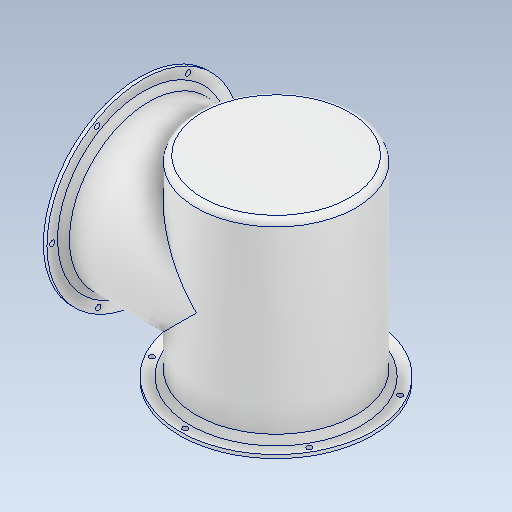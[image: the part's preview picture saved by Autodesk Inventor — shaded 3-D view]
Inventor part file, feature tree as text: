
AUTODESK INVENTOR PART (.ipt)
format: ipt  version: 2021 (Build 250183000, 183)  size: 356,352 bytes
history: native  units: mm
features: sketch x9, extrude x8, revolve x3, hole x3, plane x2, projected_geometry x2, fillet x1
ambient origin geometry x8: Origin, YZ Plane, XZ Plane, XY Plane, X Axis, Y Axis, Z Axis, Center Point
bodies: Solid1 (feature_tree)
feature tree (28):
  revolve  "Revolution1"  [1 undecoded]
  hole  "Hole1"  [1 undecoded]
  fillet  "Fillet1"  [1 undecoded]
  plane  "Work Plane1"
  sketch  "Sketch6"  dims[d10=16.0mm d11=3.0mm]
  extrude  "Extrusion3"  Depth=3.0mm
  extrude  "Extrusion5"  Depth=8.0mm
  extrude  "Extrusion4"  Depth=10.0mm
  revolve  "Revolution2"  [1 undecoded]
  extrude  "Extrusion6"  Depth=165.0mm
  hole  "Hole2"  [1 undecoded]
  extrude  "Extrusion7"  Depth=3.0mm TaperAngle=0.0deg
  plane  "Work Plane2"
  sketch  "Sketch12"  dims[d22=4.5mm d23=10.0mm d24=9.4mm d25=2.0mm d26=90.0deg d27=13.0mm d28=20.594885mm d29=4.5mm]
  extrude  "Extrusion9"  Depth=3.0mm TaperAngle=0.0deg
  extrude  "Extrusion10"  Depth=67.5mm
  extrude  "Extrusion11"  TaperAngle=90.0deg  [1 undecoded]
  revolve  "Revolution3"  [1 undecoded]
  hole  "Hole3"  [1 undecoded]
  sketch  "Sketch2"  dims[d3=90.0deg d5=81.5mm]
  projected_geometry  "Projected Loop1"
  sketch  "Sketch5"  dims[d7=9.0mm d8=5.0mm d9=45.0deg]
  projected_geometry  "Projected Loop6"
  sketch  "Sketch9"  dims[d16=4.5mm d17=8.0mm]
  sketch  "Sketch11"  dims[d18=60.0mm d20=360.0deg]
  sketch  "Sketch14"  dims[d32=2.0mm d33=5.0mm]
  sketch  "Sketch15"  dims[d34=165.0mm d43=9.0mm]
  sketch  "Sketch16"  dims[d50=135.0mm d51=10.0mm d52=0.0mm d53=112.0mm d54=0.0mm d56=48.0mm d57=0.0mm d59=67.5mm d60=90.0deg d62=5.0mm d63=45.0deg d65=48.0mm d66=0.0mm d67=48.0mm d68=0.0mm d74=2.0mm d75=3.0mm d76=67.5mm d78=2.0mm d79=4.5mm d80=4.5mm d81=60.0mm d83=360.0deg d85=4.5mm d86=6.0mm d87=6.3mm d88=2.0mm d89=90.0deg d90=8.0mm d91=20.594885mm d92=75.0mm d93=135.0mm d95=72.0mm d96=10.0mm d97=0.0mm d98=35.0mm d99=0.0mm d100=2.0mm d101=48.0mm d102=0.0mm d103=9.0mm d105=5.0mm d106=45.0deg d107=3.0mm d109=67.5mm d110=67.5mm d111=90.0deg d112=4.5mm d113=4.5mm d114=60.0mm d116=360.0deg d118=4.5mm d119=6.0mm d120=9.4mm d121=2.0mm d122=90.0deg d123=8.0mm d124=20.594885mm d125=3.0mm]
note: 8 required parameter values undecoded (feature->parameter linkage not recoverable at this tier; creation-order binding heuristic only, values carry confidence <= 0.55)